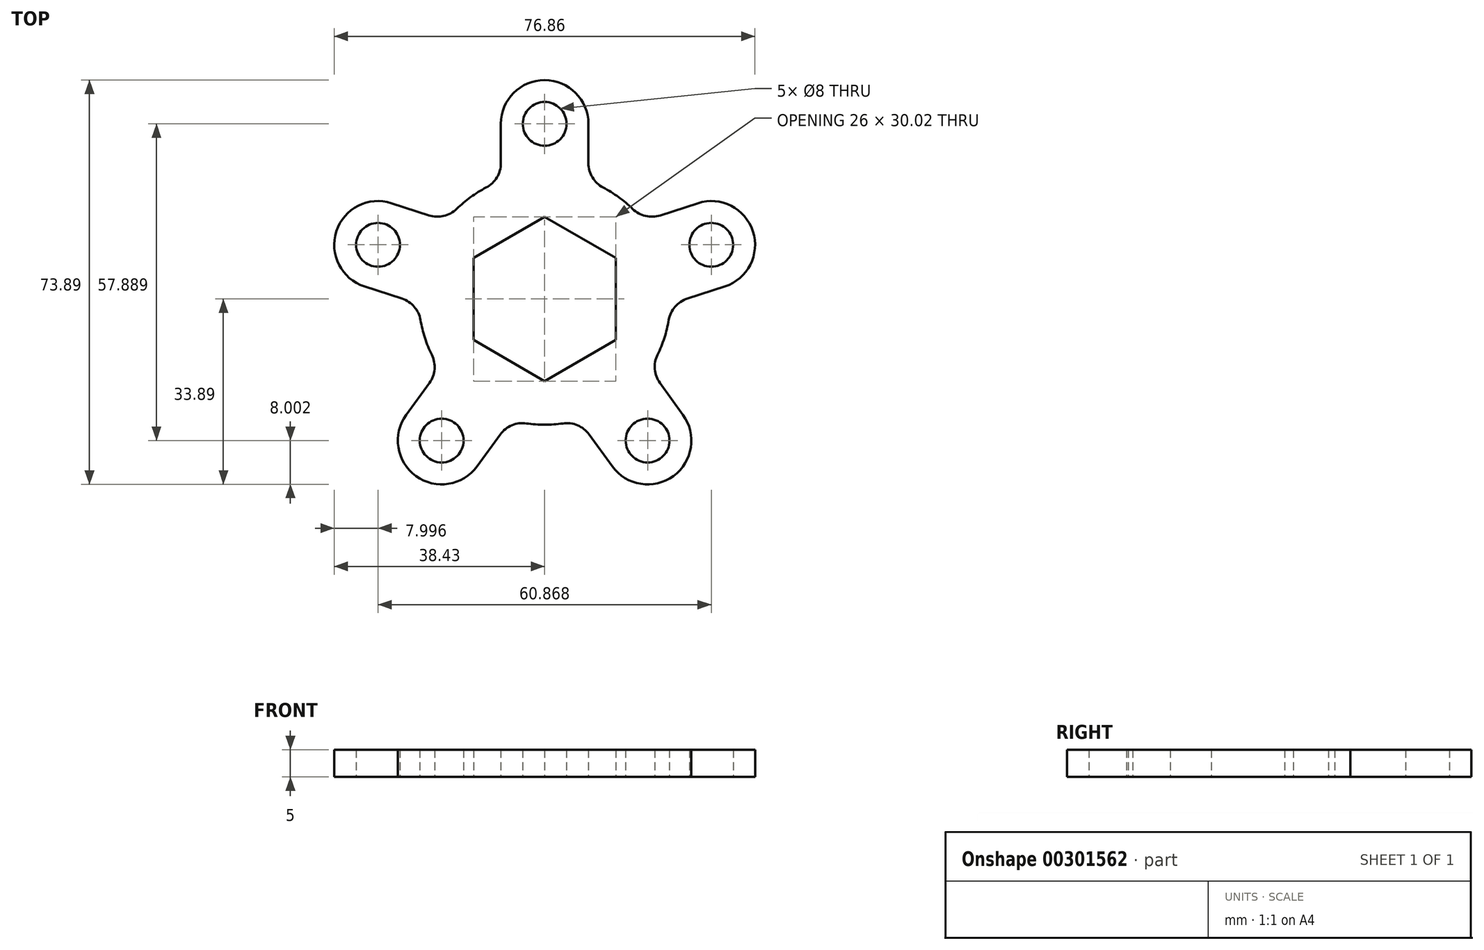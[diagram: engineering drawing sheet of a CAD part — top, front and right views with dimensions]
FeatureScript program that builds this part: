
annotation { "Feature Type Name" : "Feature", "Feature Type Description" : "" }
export const myFeature = defineFeature(function(context is Context, id is Id, definition is map)
    precondition{}
    {
        {
            var Q0;
            Q0=qCreatedBy(makeId("Top.planeOp"),FACE);
            var sketch = newSketch(context, id + "F0", { "sketchPlane" : qUnion([Q0])});
            skCircle(sketch, "E0.cCircle", {"center": v(0, 0) * mm, "radius": 13 * mm, "construction": true});
            skLineSegment(sketch, "E0.0", {"start": v(-13, -7.5) * mm, "end": v(-13, 7.5) * mm});
            skLineSegment(sketch, "E0.1", {"start": v(-13, 7.5) * mm, "end": v(0, 15.01) * mm});
            skLineSegment(sketch, "E0.2", {"start": v(0, 15.01) * mm, "end": v(13, 7.5) * mm});
            skLineSegment(sketch, "E0.3", {"start": v(13, 7.5) * mm, "end": v(13, -7.5) * mm});
            skLineSegment(sketch, "E0.4", {"start": v(13, -7.5) * mm, "end": v(0, -15.01) * mm});
            skLineSegment(sketch, "E0.5", {"start": v(0, -15.01) * mm, "end": v(-13, -7.5) * mm});
            skPoint(sketch, "E0.0.midPoint", {"position": v(-13, 0) * mm});
            skCircle(sketch, "E1", {"center": v(0, 0) * mm, "radius": 32 * mm, "construction": true});
            skCircle(sketch, "E2", {"center": v(0, 32) * mm, "radius": 4 * mm});
            skCircle(sketch, "E3.1.0", {"center": v(-30.43, 9.89) * mm, "radius": 4 * mm});
            skCircle(sketch, "E3.2.0", {"center": v(-18.8, -25.89) * mm, "radius": 4 * mm});
            skCircle(sketch, "E3.3.0", {"center": v(18.8, -25.89) * mm, "radius": 4 * mm});
            skCircle(sketch, "E3.4.0", {"center": v(30.43, 9.89) * mm, "radius": 4 * mm});
            skLineSegment(sketch, "E4", {"start": v(-10.9, 32) * mm, "end": v(12.23, 32) * mm, "construction": true});
            skArc(sketch, "E5", {"start": v(8, 32) * mm, "mid": v(0, 40) * mm, "end": v(-8, 32) * mm});
            skArc(sketch, "E6", {"start": v(-22.67, -3.86) * mm, "mid": v(-21.87, -7.1) * mm, "end": v(-20.61, -10.2) * mm});
            skLineSegment(sketch, "E7", {"start": v(-8, 32) * mm, "end": v(-8, 24.8) * mm});
            skLineSegment(sketch, "E8", {"start": v(8, 32) * mm, "end": v(8, 24.8) * mm});
            skLineSegment(sketch, "E9.1.0", {"start": v(-32.9, 2.28) * mm, "end": v(-26.06, 0.05) * mm});
            skLineSegment(sketch, "E9.1.1", {"start": v(-27.96, 17.5) * mm, "end": v(-21.11, 15.27) * mm});
            skArc(sketch, "E9.1.2", {"start": v(-27.96, 17.5) * mm, "mid": v(-38.04, 12.36) * mm, "end": v(-32.9, 2.28) * mm});
            skLineSegment(sketch, "E9.2.0", {"start": v(-12.34, -30.6) * mm, "end": v(-8.1, -24.77) * mm});
            skLineSegment(sketch, "E9.2.1", {"start": v(-25.28, -21.19) * mm, "end": v(-21.05, -15.36) * mm});
            skArc(sketch, "E9.2.2", {"start": v(-25.28, -21.19) * mm, "mid": v(-23.51, -32.36) * mm, "end": v(-12.34, -30.6) * mm});
            skLineSegment(sketch, "E9.3.0", {"start": v(25.28, -21.19) * mm, "end": v(21.05, -15.36) * mm});
            skLineSegment(sketch, "E9.3.1", {"start": v(12.34, -30.6) * mm, "end": v(8.1, -24.77) * mm});
            skArc(sketch, "E9.3.2", {"start": v(12.34, -30.6) * mm, "mid": v(23.51, -32.36) * mm, "end": v(25.28, -21.19) * mm});
            skLineSegment(sketch, "E9.4.0", {"start": v(27.96, 17.5) * mm, "end": v(21.11, 15.27) * mm});
            skLineSegment(sketch, "E9.4.1", {"start": v(32.9, 2.28) * mm, "end": v(26.06, 0.05) * mm});
            skArc(sketch, "E9.4.2", {"start": v(32.9, 2.28) * mm, "mid": v(38.04, 12.36) * mm, "end": v(27.96, 17.5) * mm});
            skArc(sketch, "E10.trimOffspring", {"start": v(-10.68, 20.37) * mm, "mid": v(-13.52, 18.6) * mm, "end": v(-16.07, 16.45) * mm});
            skArc(sketch, "E11.trimOffspring", {"start": v(16.07, 16.45) * mm, "mid": v(13.52, 18.6) * mm, "end": v(10.68, 20.37) * mm});
            skArc(sketch, "E12.trimOffspring", {"start": v(20.61, -10.2) * mm, "mid": v(21.87, -7.1) * mm, "end": v(22.67, -3.86) * mm});
            skArc(sketch, "E13.trimOffspring", {"start": v(-3.33, -22.76) * mm, "mid": v(0, -23) * mm, "end": v(3.33, -22.76) * mm});
            skPoint(sketch, "E14.visualSharp", {"position": v(-18.04, 14.27) * mm});
            skArc(sketch, "E14.filletArc", {"start": v(-21.11, 15.27) * mm, "mid": v(-18.43, 15.16) * mm, "end": v(-16.07, 16.45) * mm});
            skPoint(sketch, "E15.visualSharp", {"position": v(-8, 21.56) * mm});
            skArc(sketch, "E15.filletArc", {"start": v(-10.68, 20.37) * mm, "mid": v(-8.72, 22.21) * mm, "end": v(-8, 24.8) * mm});
            skPoint(sketch, "E16.visualSharp", {"position": v(8, 21.56) * mm});
            skArc(sketch, "E16.filletArc", {"start": v(8, 24.8) * mm, "mid": v(8.72, 22.21) * mm, "end": v(10.68, 20.37) * mm});
            skPoint(sketch, "E17.visualSharp", {"position": v(18.04, 14.27) * mm});
            skArc(sketch, "E17.filletArc", {"start": v(16.07, 16.45) * mm, "mid": v(18.43, 15.16) * mm, "end": v(21.11, 15.27) * mm});
            skPoint(sketch, "E18.visualSharp", {"position": v(22.98, -0.94) * mm});
            skArc(sketch, "E18.filletArc", {"start": v(26.06, 0.05) * mm, "mid": v(23.82, -1.43) * mm, "end": v(22.67, -3.86) * mm});
            skPoint(sketch, "E19.visualSharp", {"position": v(19.15, -12.74) * mm});
            skArc(sketch, "E19.filletArc", {"start": v(20.61, -10.2) * mm, "mid": v(20.11, -12.84) * mm, "end": v(21.05, -15.36) * mm});
            skPoint(sketch, "E20.visualSharp", {"position": v(6.2, -22.15) * mm});
            skArc(sketch, "E20.filletArc", {"start": v(8.1, -24.77) * mm, "mid": v(6, -23.1) * mm, "end": v(3.33, -22.76) * mm});
            skPoint(sketch, "E21.visualSharp", {"position": v(-6.2, -22.15) * mm});
            skArc(sketch, "E21.filletArc", {"start": v(-3.33, -22.76) * mm, "mid": v(-6, -23.1) * mm, "end": v(-8.1, -24.77) * mm});
            skPoint(sketch, "E22.visualSharp", {"position": v(-19.15, -12.74) * mm});
            skArc(sketch, "E22.filletArc", {"start": v(-21.05, -15.36) * mm, "mid": v(-20.11, -12.84) * mm, "end": v(-20.61, -10.2) * mm});
            skPoint(sketch, "E23.visualSharp", {"position": v(-22.98, -0.94) * mm});
            skArc(sketch, "E23.filletArc", {"start": v(-22.67, -3.86) * mm, "mid": v(-23.82, -1.43) * mm, "end": v(-26.06, 0.05) * mm});
            skSolve(sketch);
        }
        {
            var Q0;
            Q0=qSketchRegion(id+"F0",true);
            extrude(context, id + "F1", {"entities" : qUnion([Q0]), "depth" : 5 * mm});
        }
    });
